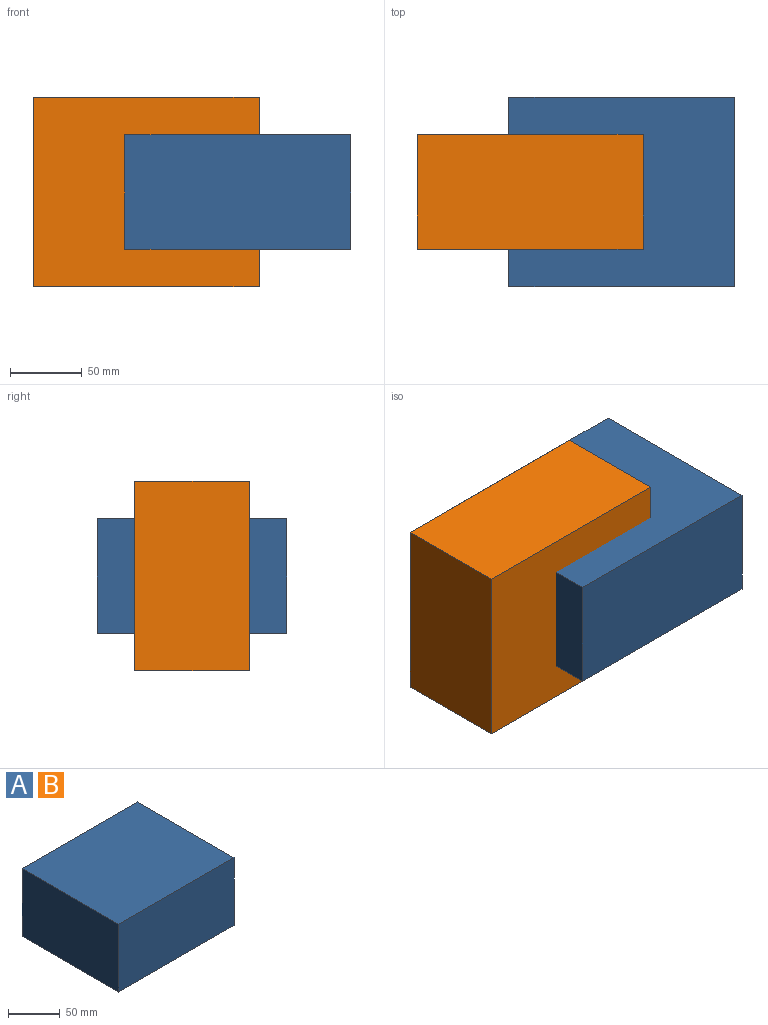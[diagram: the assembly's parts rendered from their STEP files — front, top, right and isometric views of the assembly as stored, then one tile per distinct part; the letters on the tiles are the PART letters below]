
ASSEMBLY  parts=2 mates=1
PART A: 6 faces, bbox 157.4x132x80 mm
  f0: plane 157.37x80mm, normal (0,1,0), area 12589.3mm2, adj f1,f3,f4,f5
  f1: plane 131.97x80mm, normal (-1,0,0), area 10557.7mm2, adj f0,f2,f4,f5
  f2: plane 157.37x80mm, normal (0,-1,0), area 12589.3mm2, adj f1,f3,f4,f5
  f3: plane 131.97x80mm, normal (1,0,0), area 10557.7mm2, adj f0,f2,f4,f5
  f4: plane 157.37x131.97mm, normal (0,0,1), area 20767.8mm2, adj f0,f1,f2,f3
  f5: plane 157.37x131.97mm, normal (0,0,-1), area 20767.8mm2, adj f0,f1,f2,f3
PART B: same geometry as A
PLACE A t=(-76.09,97.64,53.93)mm
PLACE B rot(axis=(1,0,0),90deg) t=(-139.95,96.07,135.5)mm
MATE slider B.f1 <-> A.f1  axis (-1,0,0) through (-211.6,56.07,93.93)mm
